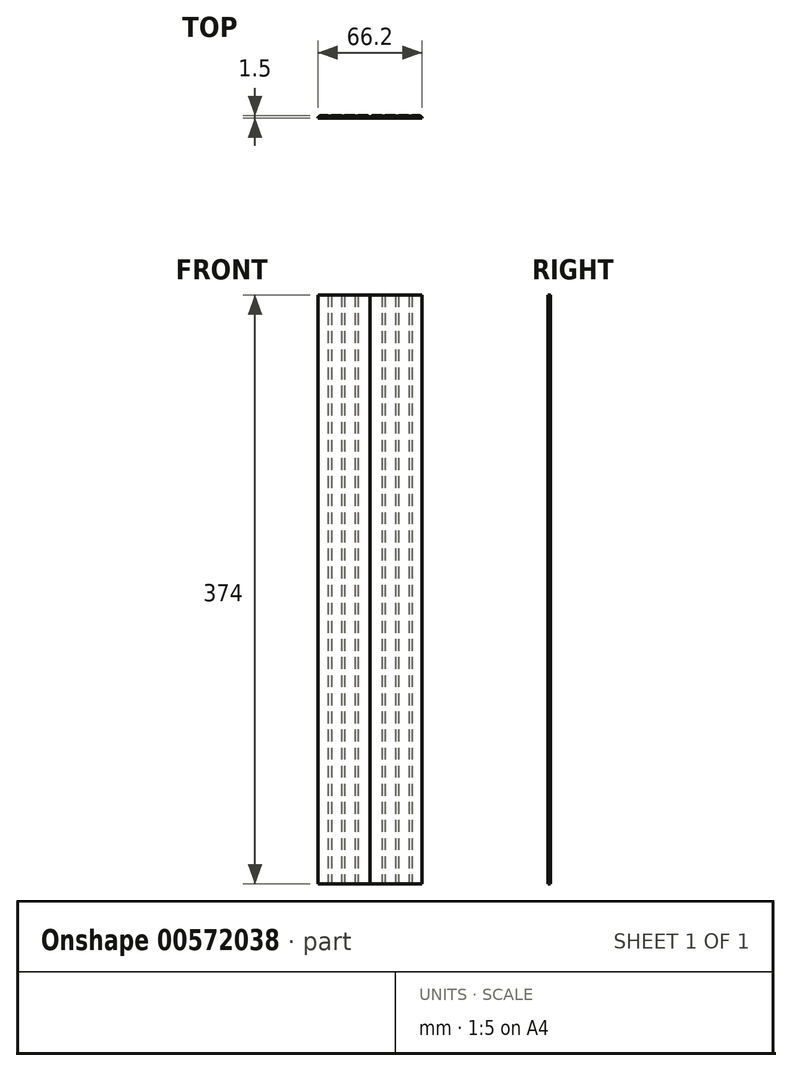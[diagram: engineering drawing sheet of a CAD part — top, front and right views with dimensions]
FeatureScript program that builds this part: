
annotation { "Feature Type Name" : "Feature", "Feature Type Description" : "" }
export const myFeature = defineFeature(function(context is Context, id is Id, definition is map)
    precondition{}
    {
        {
            var Q0;
            Q0=qCreatedBy(makeId("Top.planeOp"),FACE);
            var sketch = newSketch(context, id + "F0", { "sketchPlane" : qUnion([Q0])});
            skLineSegment(sketch, "E0", {"start": v(0, 0) * mm, "end": v(0, 7.5) * mm});
            skPoint(sketch, "E1.visualSharp", {"position": v(0, 36) * mm});
            skArc(sketch, "E1.filletArc", {"start": v(0.59, 35.41) * mm, "mid": v(0.15, 34.77) * mm, "end": v(0, 34) * mm});
            skLineSegment(sketch, "E2.1", {"start": v(1.5, 0) * mm, "end": v(1.5, 33.5) * mm});
            skLineSegment(sketch, "E3", {"start": v(1.5, 0) * mm, "end": v(0, 0) * mm});
            skPoint(sketch, "E4.visualSharp", {"position": v(1.5, 34.5) * mm});
            skArc(sketch, "E4.filletArc", {"start": v(1.8, 34.2) * mm, "mid": v(1.58, 33.88) * mm, "end": v(1.5, 33.5) * mm});
            skLineSegment(sketch, "E5.bottom", {"start": v(0, 18) * mm, "end": v(0.25, 18) * mm});
            skLineSegment(sketch, "E5.top", {"start": v(0, 16) * mm, "end": v(0.25, 16) * mm});
            skLineSegment(sketch, "E5.right", {"start": v(0.25, 18) * mm, "end": v(0.25, 16) * mm});
            skPoint(sketch, "E5.middle", {"position": v(0, 17) * mm});
            skLineSegment(sketch, "E6", {"start": v(0, 0) * mm, "end": v(-1.84, 0) * mm, "construction": true});
            skLineSegment(sketch, "E7", {"start": v(-1.84, 0) * mm, "end": v(-1.84, 17) * mm, "construction": true});
            skPoint(sketch, "E7.endSnap0", {"position": v(-0.25, 17) * mm});
            skLineSegment(sketch, "E8", {"start": v(-1.84, 8.5) * mm, "end": v(0, 8.5) * mm, "construction": true});
            skLineSegment(sketch, "E9.bottom", {"start": v(0.25, 9.5) * mm, "end": v(0, 9.5) * mm});
            skLineSegment(sketch, "E9.top", {"start": v(0.25, 7.5) * mm, "end": v(0, 7.5) * mm});
            skLineSegment(sketch, "E9.left", {"start": v(0.25, 9.5) * mm, "end": v(0.25, 7.5) * mm});
            skPoint(sketch, "E9.middle", {"position": v(0, 8.5) * mm});
            skLineSegment(sketch, "E10", {"start": v(-1.84, 17) * mm, "end": v(-1.84, 34) * mm, "construction": true});
            skLineSegment(sketch, "E11", {"start": v(-1.84, 25.5) * mm, "end": v(0, 25.5) * mm, "construction": true});
            skLineSegment(sketch, "E12.bottom", {"start": v(0.25, 26.5) * mm, "end": v(0, 26.5) * mm});
            skLineSegment(sketch, "E12.top", {"start": v(0.25, 24.5) * mm, "end": v(0, 24.5) * mm});
            skLineSegment(sketch, "E12.left", {"start": v(0.25, 26.5) * mm, "end": v(0.25, 24.5) * mm});
            skPoint(sketch, "E12.middle", {"position": v(0, 25.5) * mm});
            skPoint(sketch, "E13.end.orphan", {"position": v(36, 36) * mm});
            skLineSegment(sketch, "E14.trimOffspring", {"start": v(0, 9.5) * mm, "end": v(0, 16) * mm});
            skPoint(sketch, "E15.orphan", {"position": v(-0.25, 9.5) * mm});
            skPoint(sketch, "E16.orphan", {"position": v(-0.25, 7.5) * mm});
            skPoint(sketch, "E17.orphan", {"position": v(-0.25, 16) * mm});
            skLineSegment(sketch, "E18.trimOffspring", {"start": v(0, 18) * mm, "end": v(0, 24.5) * mm});
            skPoint(sketch, "E19.orphan", {"position": v(-0.25, 18) * mm});
            skLineSegment(sketch, "E20.trimOffspring", {"start": v(0, 26.5) * mm, "end": v(0, 34) * mm});
            skPoint(sketch, "E21.orphan", {"position": v(-0.25, 24.5) * mm});
            skPoint(sketch, "E22.orphan", {"position": v(-0.25, 26.5) * mm});
            skLineSegment(sketch, "E23.MirrorCS", {"start": v(11.5, 35.75) * mm, "end": v(11.5, 36) * mm});
            skLineSegment(sketch, "E24.MirrorCS", {"start": v(26.5, 35.75) * mm, "end": v(28.5, 35.75) * mm});
            skLineSegment(sketch, "E25.MirrorCS", {"start": v(28.5, 35.75) * mm, "end": v(28.5, 36) * mm});
            skLineSegment(sketch, "E26.MirrorCS", {"start": v(9.5, 35.75) * mm, "end": v(11.5, 35.75) * mm});
            skLineSegment(sketch, "E27.MirrorCS", {"start": v(9.5, 35.75) * mm, "end": v(9.5, 36) * mm});
            skLineSegment(sketch, "E28.MirrorCS", {"start": v(20, 36) * mm, "end": v(20, 35.75) * mm});
            skLineSegment(sketch, "E29.MirrorCS", {"start": v(26.5, 35.75) * mm, "end": v(26.5, 36) * mm});
            skLineSegment(sketch, "E30.MirrorCS", {"start": v(18, 35.75) * mm, "end": v(20, 35.75) * mm});
            skLineSegment(sketch, "E31.MirrorCS", {"start": v(18, 36) * mm, "end": v(18, 35.75) * mm});
            skArc(sketch, "E32.MirrorCS", {"start": v(1.8, 34.2) * mm, "mid": v(2.12, 34.42) * mm, "end": v(2.5, 34.5) * mm});
            skLineSegment(sketch, "E33.MirrorCS", {"start": v(36, 34.5) * mm, "end": v(36, 36) * mm});
            skArc(sketch, "E34.MirrorCS", {"start": v(0.59, 35.41) * mm, "mid": v(1.23, 35.85) * mm, "end": v(2, 36) * mm});
            skLineSegment(sketch, "E35.MirrorCS", {"start": v(10.5, 37.84) * mm, "end": v(10.5, 36) * mm, "construction": true});
            skLineSegment(sketch, "E36.MirrorCS", {"start": v(36, 36) * mm, "end": v(36, 37.84) * mm, "construction": true});
            skPoint(sketch, "E37.MirrorP", {"position": v(19, 36.25) * mm});
            skLineSegment(sketch, "E38.MirrorCS", {"start": v(27.5, 37.84) * mm, "end": v(27.5, 36) * mm, "construction": true});
            skPoint(sketch, "E39.MirrorP", {"position": v(19, 36) * mm});
            skLineSegment(sketch, "E40.MirrorCS", {"start": v(36, 34.5) * mm, "end": v(2.5, 34.5) * mm});
            skPoint(sketch, "E41.MirrorP", {"position": v(27.5, 36) * mm});
            skLineSegment(sketch, "E42.MirrorCS", {"start": v(36, 36) * mm, "end": v(28.5, 36) * mm});
            skLineSegment(sketch, "E43.MirrorCS", {"start": v(19, 37.84) * mm, "end": v(2, 37.84) * mm, "construction": true});
            skPoint(sketch, "E44.MirrorP", {"position": v(28.5, 36.25) * mm});
            skLineSegment(sketch, "E45.MirrorCS", {"start": v(18, 36) * mm, "end": v(11.5, 36) * mm});
            skPoint(sketch, "E46.MirrorP", {"position": v(18, 36.25) * mm});
            skPoint(sketch, "E47.MirrorP", {"position": v(10.5, 36) * mm});
            skPoint(sketch, "E48.MirrorP", {"position": v(9.5, 36.25) * mm});
            skPoint(sketch, "E49.MirrorP", {"position": v(20, 36.25) * mm});
            skPoint(sketch, "E50.MirrorP", {"position": v(26.5, 36.25) * mm});
            skLineSegment(sketch, "E51.MirrorCS", {"start": v(9.5, 36) * mm, "end": v(2, 36) * mm});
            skLineSegment(sketch, "E52.MirrorCS", {"start": v(36, 37.84) * mm, "end": v(19, 37.84) * mm, "construction": true});
            skPoint(sketch, "E53.MirrorP", {"position": v(11.5, 36.25) * mm});
            skLineSegment(sketch, "E54.MirrorCS", {"start": v(26.5, 36) * mm, "end": v(20, 36) * mm});
            skSolve(sketch);
        }
        {
            var Q0;
            Q0=qSketchRegion(id+"F0",true);
            extrude(context, id + "F1", {"entities" : qUnion([Q0]), "depth" : 704 * mm, "offsetDistance" : 25 * mm});
        }
        {
            var Q0;
            Q0=makeQuery(id+"F1.opExtrude","CAP_FACE",FACE,{"disambiguationData":[OSD([sQuery(id+"F0.wireOp",EDGE,"E0"),sQuery(id+"F0.wireOp",EDGE,"E1.filletArc"),sQuery(id+"F0.wireOp",EDGE,"E2.1"),sQuery(id+"F0.wireOp",EDGE,"E3"),sQuery(id+"F0.wireOp",EDGE,"E4.filletArc"),sQuery(id+"F0.wireOp",EDGE,"E5.bottom"),sQuery(id+"F0.wireOp",EDGE,"E5.top"),sQuery(id+"F0.wireOp",EDGE,"E5.right"),sQuery(id+"F0.wireOp",EDGE,"E9.bottom"),sQuery(id+"F0.wireOp",EDGE,"E9.top"),sQuery(id+"F0.wireOp",EDGE,"E9.left"),sQuery(id+"F0.wireOp",EDGE,"E12.bottom"),sQuery(id+"F0.wireOp",EDGE,"E12.top"),sQuery(id+"F0.wireOp",EDGE,"E12.left"),sQuery(id+"F0.wireOp",EDGE,"E14.trimOffspring"),sQuery(id+"F0.wireOp",EDGE,"E18.trimOffspring"),sQuery(id+"F0.wireOp",EDGE,"E20.trimOffspring"),sQuery(id+"F0.wireOp",EDGE,"E23.MirrorCS"),sQuery(id+"F0.wireOp",EDGE,"E24.MirrorCS"),sQuery(id+"F0.wireOp",EDGE,"E25.MirrorCS"),sQuery(id+"F0.wireOp",EDGE,"E26.MirrorCS"),sQuery(id+"F0.wireOp",EDGE,"E27.MirrorCS"),sQuery(id+"F0.wireOp",EDGE,"E28.MirrorCS"),sQuery(id+"F0.wireOp",EDGE,"E29.MirrorCS"),sQuery(id+"F0.wireOp",EDGE,"E30.MirrorCS"),sQuery(id+"F0.wireOp",EDGE,"E31.MirrorCS"),sQuery(id+"F0.wireOp",EDGE,"E32.MirrorCS"),sQuery(id+"F0.wireOp",EDGE,"E33.MirrorCS"),sQuery(id+"F0.wireOp",EDGE,"E34.MirrorCS"),sQuery(id+"F0.wireOp",EDGE,"E40.MirrorCS"),sQuery(id+"F0.wireOp",EDGE,"E42.MirrorCS"),sQuery(id+"F0.wireOp",EDGE,"E45.MirrorCS"),sQuery(id+"F0.wireOp",EDGE,"E51.MirrorCS"),sQuery(id+"F0.wireOp",EDGE,"E54.MirrorCS")])],"isStart":false});
            var sketch = newSketch(context, id + "F2", { "sketchPlane" : qUnion([Q0])});
            skLineSegment(sketch, "E55.bottom", {"start": v(0, 0) * mm, "end": v(3, 0) * mm});
            skLineSegment(sketch, "E55.top", {"start": v(0, 37.06) * mm, "end": v(3, 37.06) * mm});
            skLineSegment(sketch, "E55.left", {"start": v(0, 0) * mm, "end": v(0, 37.06) * mm});
            skLineSegment(sketch, "E55.right", {"start": v(3, 0) * mm, "end": v(3, 37.06) * mm});
            skSolve(sketch);
        }
        {
            var Q0;
            {var subQ4=sQuery(id+"F2.wireOp",EDGE,"E55.top");Q0=makeQuery(id+"F2.imprint","IMPRINT",FACE,{"disambiguationData":[TD([[makeQuery(id+"F2.imprint","IMPRINT",EDGE,{"derivedFrom":subQ4}),-1.0]])]});}
            var Q1;
            {var subQ4=sQuery(id+"F0.wireOp",EDGE,"E2.1");Q1=makeQuery(id+"F2.imprint","IMPRINT",FACE,{"disambiguationData":[TD([[makeQuery(id+"F2.imprint","IMPRINT",EDGE,{"derivedFrom":makeQuery(id+"F1.opExtrude","CAP_EDGE",EDGE,{"disambiguationData":[OSD([subQ4])],"isStart":false})}),-1.0]])]});}
            var Q2;
            {var subQ13=sQuery(id+"F0.wireOp",EDGE,"E5.right");Q2=makeQuery(id+"F2.imprint","IMPRINT",FACE,{"disambiguationData":[TD([[makeQuery(id+"F2.imprint","IMPRINT",EDGE,{"derivedFrom":makeQuery(id+"F1.opExtrude","CAP_EDGE",EDGE,{"disambiguationData":[OSD([subQ13])],"isStart":false})}),1.0]])]});}
            extrude(context, id + "F3", {"entities" : qUnion([Q0, Q1, Q2]), "operationType" : NewBodyOperationType.REMOVE, "endBound" : BoundingType.THROUGH_ALL, "oppositeDirection" : true, "depth" : 25 * mm, "offsetDistance" : 25 * mm});
        }
        {
            var Q0;
            Q0=makeQuery(id+"F3.boolean.opBoolean","INTERSECT",EDGE,{"derivedFrom":[makeQuery(id+"F1.opExtrude","SWEPT_FACE",FACE,{"disambiguationData":[OSD([sQuery(id+"F0.wireOp",EDGE,"E51.MirrorCS")])]}),makeQuery(id+"F3.opExtrude","SWEPT_FACE",FACE,{"disambiguationData":[OSD([sQuery(id+"F2.wireOp",EDGE,"E55.right")])]})]});
            var Q1;
            Q1=makeQuery(id+"F1.opExtrude","SWEPT_EDGE",EDGE,{"disambiguationData":[OSD([sQuery(id+"F0.wireOp",EDGE,"E33.MirrorCS"),sQuery(id+"F0.wireOp",EDGE,"E42.MirrorCS")])]});
            fillet(context, id + "F4", {"entities" : qUnion([Q0, Q1]), "radius" : 2 * mm, "tangentPropagation" : true, "allowEdgeOverflow" : false});
        }
        {
            var Q0;
            Q0=makeQuery(id+"F1.opExtrude","SWEPT_EDGE",EDGE,{"disambiguationData":[OSD([sQuery(id+"F0.wireOp",EDGE,"E31.MirrorCS"),sQuery(id+"F0.wireOp",EDGE,"E45.MirrorCS")])]});
            var Q1;
            Q1=makeQuery(id+"F1.opExtrude","SWEPT_EDGE",EDGE,{"disambiguationData":[OSD([sQuery(id+"F0.wireOp",EDGE,"E28.MirrorCS"),sQuery(id+"F0.wireOp",EDGE,"E54.MirrorCS")])]});
            var Q2;
            Q2=makeQuery(id+"F1.opExtrude","SWEPT_EDGE",EDGE,{"disambiguationData":[OSD([sQuery(id+"F0.wireOp",EDGE,"E25.MirrorCS"),sQuery(id+"F0.wireOp",EDGE,"E42.MirrorCS")])]});
            var Q3;
            Q3=makeQuery(id+"F1.opExtrude","SWEPT_EDGE",EDGE,{"disambiguationData":[OSD([sQuery(id+"F0.wireOp",EDGE,"E29.MirrorCS"),sQuery(id+"F0.wireOp",EDGE,"E54.MirrorCS")])]});
            var Q4;
            Q4=makeQuery(id+"F1.opExtrude","SWEPT_EDGE",EDGE,{"disambiguationData":[OSD([sQuery(id+"F0.wireOp",EDGE,"E27.MirrorCS"),sQuery(id+"F0.wireOp",EDGE,"E51.MirrorCS")])]});
            var Q5;
            Q5=makeQuery(id+"F1.opExtrude","SWEPT_EDGE",EDGE,{"disambiguationData":[OSD([sQuery(id+"F0.wireOp",EDGE,"E23.MirrorCS"),sQuery(id+"F0.wireOp",EDGE,"E45.MirrorCS")])]});
            fillet(context, id + "F5", {"entities" : qUnion([Q0, Q1, Q2, Q3, Q4, Q5]), "radius" : 0.2 * mm, "tangentPropagation" : true, "allowEdgeOverflow" : false});
        }
        {
            var Q0;
            Q0=qCreatedBy(makeId("Right.planeOp"),FACE);
            cPlane(context, id + "F6", {"entities" : qUnion([Q0]), "cplaneType" : CPlaneType.OFFSET, "offset" : 36.1 * mm, "width" : 150 * mm, "height" : 150 * mm});
        }
        {
            var Q0;
            Q0=makeQuery(id+"F1.opExtrude","SWEPT_BODY",BODY,{"disambiguationData":[OSD([sQuery(id+"F0.wireOp",EDGE,"E0"),sQuery(id+"F0.wireOp",EDGE,"E1.filletArc"),sQuery(id+"F0.wireOp",EDGE,"E2.1"),sQuery(id+"F0.wireOp",EDGE,"E3"),sQuery(id+"F0.wireOp",EDGE,"E4.filletArc"),sQuery(id+"F0.wireOp",EDGE,"E5.bottom"),sQuery(id+"F0.wireOp",EDGE,"E5.top"),sQuery(id+"F0.wireOp",EDGE,"E5.right"),sQuery(id+"F0.wireOp",EDGE,"E9.bottom"),sQuery(id+"F0.wireOp",EDGE,"E9.top"),sQuery(id+"F0.wireOp",EDGE,"E9.left"),sQuery(id+"F0.wireOp",EDGE,"E12.bottom"),sQuery(id+"F0.wireOp",EDGE,"E12.top"),sQuery(id+"F0.wireOp",EDGE,"E12.left"),sQuery(id+"F0.wireOp",EDGE,"E14.trimOffspring"),sQuery(id+"F0.wireOp",EDGE,"E18.trimOffspring"),sQuery(id+"F0.wireOp",EDGE,"E20.trimOffspring"),sQuery(id+"F0.wireOp",EDGE,"E23.MirrorCS"),sQuery(id+"F0.wireOp",EDGE,"E24.MirrorCS"),sQuery(id+"F0.wireOp",EDGE,"E25.MirrorCS"),sQuery(id+"F0.wireOp",EDGE,"E26.MirrorCS"),sQuery(id+"F0.wireOp",EDGE,"E27.MirrorCS"),sQuery(id+"F0.wireOp",EDGE,"E28.MirrorCS"),sQuery(id+"F0.wireOp",EDGE,"E29.MirrorCS"),sQuery(id+"F0.wireOp",EDGE,"E30.MirrorCS"),sQuery(id+"F0.wireOp",EDGE,"E31.MirrorCS"),sQuery(id+"F0.wireOp",EDGE,"E32.MirrorCS"),sQuery(id+"F0.wireOp",EDGE,"E33.MirrorCS"),sQuery(id+"F0.wireOp",EDGE,"E34.MirrorCS"),sQuery(id+"F0.wireOp",EDGE,"E40.MirrorCS"),sQuery(id+"F0.wireOp",EDGE,"E42.MirrorCS"),sQuery(id+"F0.wireOp",EDGE,"E45.MirrorCS"),sQuery(id+"F0.wireOp",EDGE,"E51.MirrorCS"),sQuery(id+"F0.wireOp",EDGE,"E54.MirrorCS")])]});
            var Q1;
            Q1=qCreatedBy(id+"F6.planeOp",FACE);
            mirror(context, id + "F7", {"operationType" : NewBodyOperationType.ADD, "entities" : qUnion([Q0]), "mirrorPlane" : qUnion([Q1])});
        }
        {
            var Q0;
            Q0=makeQuery(id+"F7.opPattern","COPY",FACE,{"derivedFrom":makeQuery(id+"F1.opExtrude","SWEPT_FACE",FACE,{"disambiguationData":[OSD([sQuery(id+"F0.wireOp",EDGE,"E40.MirrorCS")])]}),"instanceName":"1"});
            var sketch = newSketch(context, id + "F8", { "sketchPlane" : qUnion([Q0])});
            skPoint(sketch, "E56.0", {"position": v(3, 704) * mm});
            skLineSegment(sketch, "E57.top", {"start": v(3, -20.96) * mm, "end": v(168.47, -20.96) * mm});
            skLineSegment(sketch, "E57.left", {"start": v(3, 330) * mm, "end": v(3, -20.96) * mm});
            skLineSegment(sketch, "E57.right", {"start": v(168.47, 330) * mm, "end": v(168.47, -20.96) * mm});
            skLineSegment(sketch, "E58", {"start": v(3, 330) * mm, "end": v(168.47, 330) * mm});
            skSolve(sketch);
        }
        {
            var Q0;
            Q0 = qSketchRegion(id + "F8", true);
            extrude(context, id + "F9", {"entities" : qUnion([Q0]), "operationType" : NewBodyOperationType.REMOVE, "endBound" : BoundingType.THROUGH_ALL, "oppositeDirection" : true, "depth" : 25 * mm, "offsetDistance" : 25 * mm});
        }
    });
